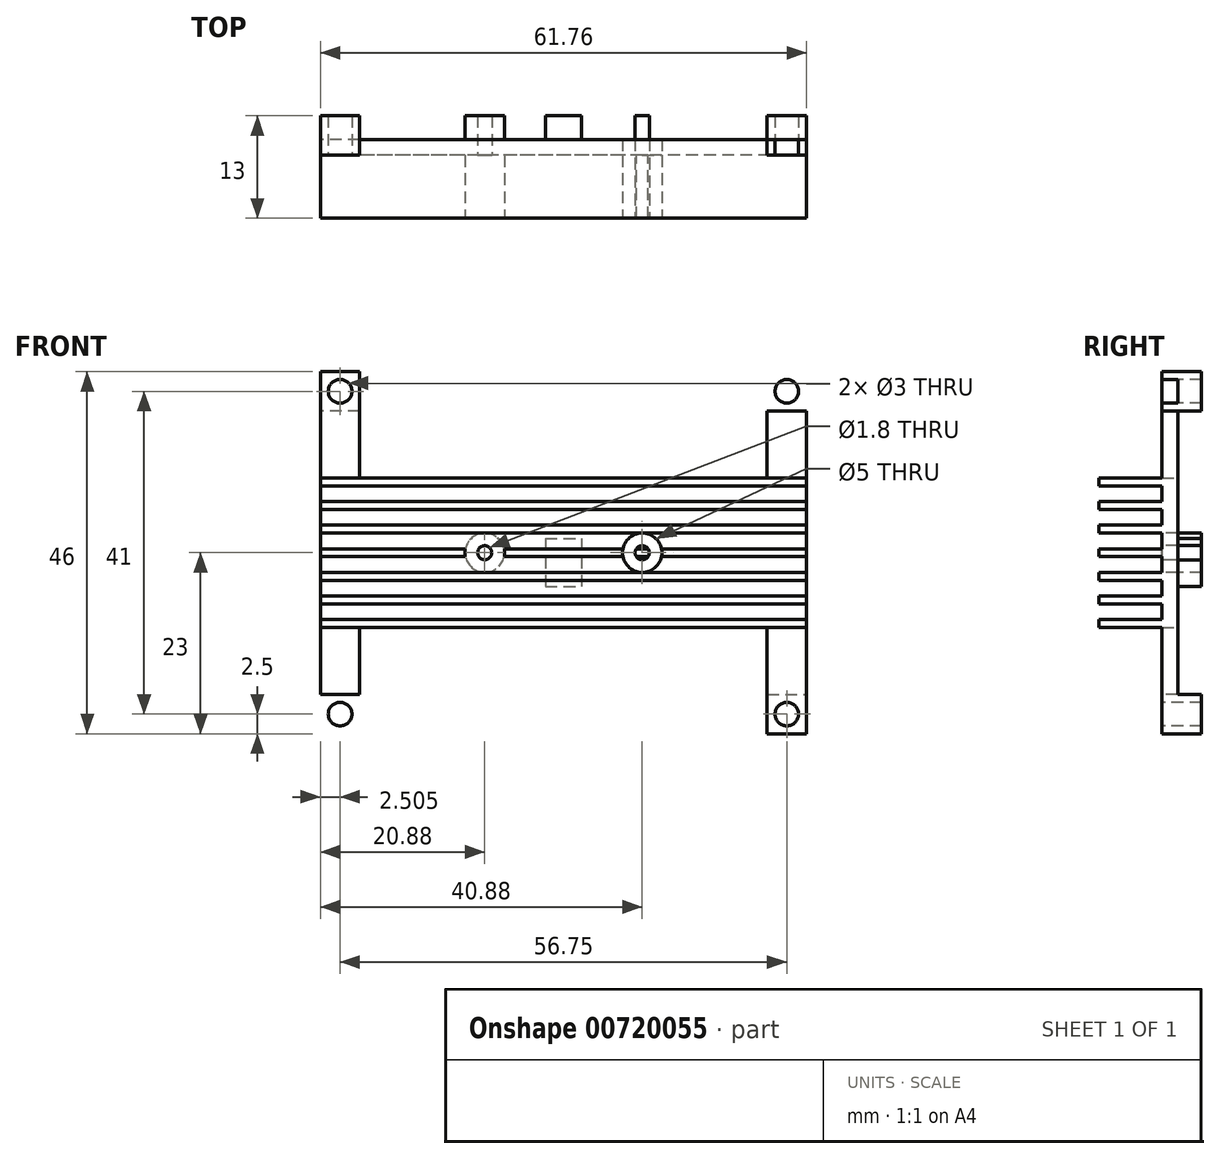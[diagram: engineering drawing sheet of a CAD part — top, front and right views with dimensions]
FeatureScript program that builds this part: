
annotation { "Feature Type Name" : "Feature", "Feature Type Description" : "" }
export const myFeature = defineFeature(function(context is Context, id is Id, definition is map)
    precondition{}
    {
        {
            var Q0;
            Q0=qCreatedBy(makeId("Front.planeOp"),FACE);
            var sketch = newSketch(context, id + "F0", { "sketchPlane" : qUnion([Q0])});
            skLineSegment(sketch, "E0", {"start": v(0, 0) * mm, "end": v(-30.88, 0) * mm, "construction": true});
            skLineSegment(sketch, "E1", {"start": v(-30.88, 0) * mm, "end": v(-30.88, 23) * mm, "construction": true});
            skLineSegment(sketch, "E2.bottom", {"start": v(-30.88, 23) * mm, "end": v(30.88, 23) * mm});
            skLineSegment(sketch, "E2.top", {"start": v(-30.88, -23) * mm, "end": v(30.88, -23) * mm});
            skLineSegment(sketch, "E2.left", {"start": v(-30.88, 23) * mm, "end": v(-30.88, -23) * mm});
            skLineSegment(sketch, "E2.right", {"start": v(30.88, 23) * mm, "end": v(30.88, -23) * mm});
            skPoint(sketch, "E2.middle", {"position": v(0, 0) * mm});
            skLineSegment(sketch, "E3", {"start": v(0, 0) * mm, "end": v(25.88, 0) * mm, "construction": true});
            skLineSegment(sketch, "E4", {"start": v(25.88, 0) * mm, "end": v(25.88, 9.5) * mm, "construction": true});
            skLineSegment(sketch, "E5", {"start": v(25.88, 9.5) * mm, "end": v(25.88, 23) * mm});
            skLineSegment(sketch, "E6", {"start": v(25.87, 9.5) * mm, "end": v(0, 9.5) * mm});
            skLineSegment(sketch, "E7.MirrorCS", {"start": v(-25.88, 9.5) * mm, "end": v(-25.88, 23) * mm});
            skLineSegment(sketch, "E8.MirrorCS", {"start": v(-25.87, 9.5) * mm, "end": v(0, 9.5) * mm});
            skLineSegment(sketch, "E9.MirrorCS", {"start": v(-25.88, -9.5) * mm, "end": v(-25.87, -23) * mm});
            skLineSegment(sketch, "E10.MirrorCS", {"start": v(-25.87, -9.5) * mm, "end": v(0, -9.5) * mm});
            skLineSegment(sketch, "E11.MirrorCS", {"start": v(25.88, -9.5) * mm, "end": v(25.88, -23) * mm});
            skLineSegment(sketch, "E12.MirrorCS", {"start": v(25.87, -9.5) * mm, "end": v(0, -9.5) * mm});
            skSolve(sketch);
        }
        {
            var Q0;
            Q0=makeQuery(id+"F0.imprint","IMPRINT",FACE,{"disambiguationData":[TD([[makeQuery(id+"F0.imprint","IMPRINT",EDGE,{"derivedFrom":sQuery(id+"F0.wireOp",EDGE,"E2.bottom")}),-1.0]])]});
            extrude(context, id + "F1", {"entities" : qUnion([Q0]), "depth" : 10 * mm, "offsetDistance" : 25 * mm});
        }
        {
            var Q0;
            Q0=makeQuery(id+"F1.opExtrude","CAP_FACE",FACE,{"disambiguationData":[OSD([sQuery(id+"F0.wireOp",EDGE,"E2.bottom"),sQuery(id+"F0.wireOp",EDGE,"E2.top"),sQuery(id+"F0.wireOp",EDGE,"E2.left"),sQuery(id+"F0.wireOp",EDGE,"E2.right")])],"isStart":false});
            var sketch = newSketch(context, id + "F2", { "sketchPlane" : qUnion([Q0])});
            skLineSegment(sketch, "E13", {"start": v(-30.88, 0) * mm, "end": v(-30.88, 0.5) * mm, "construction": true});
            skLineSegment(sketch, "E14.bottom", {"start": v(-30.88, 0.5) * mm, "end": v(30.88, 0.5) * mm});
            skLineSegment(sketch, "E14.top", {"start": v(-30.88, -0.5) * mm, "end": v(30.88, -0.5) * mm});
            skLineSegment(sketch, "E14.left", {"start": v(-30.88, 0.5) * mm, "end": v(-30.88, -0.5) * mm});
            skLineSegment(sketch, "E14.right", {"start": v(30.88, 0.5) * mm, "end": v(30.88, -0.5) * mm});
            skPoint(sketch, "E14.middle", {"position": v(0, 0) * mm});
            skLineSegment(sketch, "E15.0.1.0", {"start": v(-30.88, 3.5) * mm, "end": v(30.88, 3.5) * mm});
            skLineSegment(sketch, "E15.0.1.1", {"start": v(-30.88, 3.5) * mm, "end": v(-30.88, 2.5) * mm});
            skLineSegment(sketch, "E15.0.1.2", {"start": v(-30.88, 2.5) * mm, "end": v(30.88, 2.5) * mm});
            skLineSegment(sketch, "E15.0.1.3", {"start": v(30.88, 3.5) * mm, "end": v(30.88, 2.5) * mm});
            skLineSegment(sketch, "E15.0.2.0", {"start": v(-30.88, 6.5) * mm, "end": v(30.88, 6.5) * mm});
            skLineSegment(sketch, "E15.0.2.1", {"start": v(-30.88, 6.5) * mm, "end": v(-30.88, 5.5) * mm});
            skLineSegment(sketch, "E15.0.2.2", {"start": v(-30.88, 5.5) * mm, "end": v(30.88, 5.5) * mm});
            skLineSegment(sketch, "E15.0.2.3", {"start": v(30.88, 6.5) * mm, "end": v(30.88, 5.5) * mm});
            skLineSegment(sketch, "E15.direction1", {"start": v(-30.88, 0.5) * mm, "end": v(-25, 0.5) * mm, "construction": true});
            skLineSegment(sketch, "E15.direction2", {"start": v(-30.88, 0.5) * mm, "end": v(-30.88, 3.5) * mm, "construction": true});
            skLineSegment(sketch, "E16.0.1.0", {"start": v(-30.88, -2.5) * mm, "end": v(30.88, -2.5) * mm});
            skLineSegment(sketch, "E16.0.1.1", {"start": v(-30.88, -2.5) * mm, "end": v(-30.88, -3.5) * mm});
            skLineSegment(sketch, "E16.0.1.2", {"start": v(-30.88, -3.5) * mm, "end": v(30.88, -3.5) * mm});
            skLineSegment(sketch, "E16.0.1.3", {"start": v(30.88, -2.5) * mm, "end": v(30.88, -3.5) * mm});
            skLineSegment(sketch, "E16.0.2.0", {"start": v(-30.88, -5.5) * mm, "end": v(30.88, -5.5) * mm});
            skLineSegment(sketch, "E16.0.2.1", {"start": v(-30.88, -5.5) * mm, "end": v(-30.88, -6.5) * mm});
            skLineSegment(sketch, "E16.0.2.2", {"start": v(-30.88, -6.5) * mm, "end": v(30.88, -6.5) * mm});
            skLineSegment(sketch, "E16.0.2.3", {"start": v(30.88, -5.5) * mm, "end": v(30.88, -6.5) * mm});
            skLineSegment(sketch, "E16.direction2", {"start": v(-30.88, 0.5) * mm, "end": v(-30.88, -2.5) * mm, "construction": true});
            skLineSegment(sketch, "E17.0.0.3", {"start": v(-30.88, 9.5) * mm, "end": v(30.88, 9.5) * mm});
            skLineSegment(sketch, "E17.3.0.3", {"start": v(-30.88, 9.5) * mm, "end": v(-30.88, 8.5) * mm});
            skLineSegment(sketch, "E17.6.0.3", {"start": v(-30.88, 8.5) * mm, "end": v(30.88, 8.5) * mm});
            skLineSegment(sketch, "E17.9.0.3", {"start": v(30.88, 9.5) * mm, "end": v(30.88, 8.5) * mm});
            skLineSegment(sketch, "E18.0.0.3", {"start": v(-30.88, -8.5) * mm, "end": v(30.88, -8.5) * mm});
            skLineSegment(sketch, "E18.3.0.3", {"start": v(-30.88, -8.5) * mm, "end": v(-30.88, -9.5) * mm});
            skLineSegment(sketch, "E18.6.0.3", {"start": v(-30.88, -9.5) * mm, "end": v(30.88, -9.5) * mm});
            skLineSegment(sketch, "E18.9.0.3", {"start": v(30.88, -8.5) * mm, "end": v(30.88, -9.5) * mm});
            skSolve(sketch);
        }
        {
            var Q0;
            Q0=qCreatedBy(makeId("Front.planeOp"),FACE);
            cPlane(context, id + "F3", {"entities" : qUnion([Q0]), "cplaneType" : CPlaneType.OFFSET, "offset" : 2 * mm, "width" : 150 * mm, "height" : 150 * mm});
        }
        {
            var Q0;
            {var subQ1=sQuery(id+"F0.wireOp",EDGE,"E7.MirrorCS");var subQ2=makeQuery(id+"F1.opExtrude","CAP_EDGE",EDGE,{"disambiguationData":[OSD([subQ1])],"isStart":false});Q0=makeQuery(id+"F2.imprint","IMPRINT",FACE,{"disambiguationData":[TD([[makeQuery(id+"F2.imprint","IMPRINT",EDGE,{"derivedFrom":subQ2}),1.0]])]});}
            var Q1;
            {var subQ0=sQuery(id+"F2.wireOp",EDGE,"E15.0.2.0");Q1=makeQuery(id+"F2.imprint","IMPRINT",FACE,{"disambiguationData":[TD([[makeQuery(id+"F2.imprint","IMPRINT",EDGE,{"derivedFrom":subQ0}),1.0]])]});}
            var Q2;
            {var subQ0=sQuery(id+"F2.wireOp",EDGE,"E15.0.1.0");Q2=makeQuery(id+"F2.imprint","IMPRINT",FACE,{"disambiguationData":[TD([[makeQuery(id+"F2.imprint","IMPRINT",EDGE,{"derivedFrom":subQ0}),1.0]])]});}
            var Q3;
            {var subQ0=sQuery(id+"F2.wireOp",EDGE,"E14.bottom");Q3=makeQuery(id+"F2.imprint","IMPRINT",FACE,{"disambiguationData":[TD([[makeQuery(id+"F2.imprint","IMPRINT",EDGE,{"derivedFrom":subQ0}),1.0]])]});}
            var Q4;
            {var subQ0=sQuery(id+"F2.wireOp",EDGE,"E14.top");Q4=makeQuery(id+"F2.imprint","IMPRINT",FACE,{"disambiguationData":[TD([[makeQuery(id+"F2.imprint","IMPRINT",EDGE,{"derivedFrom":subQ0}),-1.0]])]});}
            var Q5;
            {var subQ0=sQuery(id+"F2.wireOp",EDGE,"E16.0.1.2");Q5=makeQuery(id+"F2.imprint","IMPRINT",FACE,{"disambiguationData":[TD([[makeQuery(id+"F2.imprint","IMPRINT",EDGE,{"derivedFrom":subQ0}),-1.0]])]});}
            var Q6;
            {var subQ0=sQuery(id+"F2.wireOp",EDGE,"E16.0.2.2");Q6=makeQuery(id+"F2.imprint","IMPRINT",FACE,{"disambiguationData":[TD([[makeQuery(id+"F2.imprint","IMPRINT",EDGE,{"derivedFrom":subQ0}),-1.0]])]});}
            var Q7;
            {var subQ1=sQuery(id+"F0.wireOp",EDGE,"E9.MirrorCS");var subQ2=makeQuery(id+"F1.opExtrude","CAP_EDGE",EDGE,{"disambiguationData":[OSD([subQ1])],"isStart":false});Q7=makeQuery(id+"F2.imprint","IMPRINT",FACE,{"disambiguationData":[TD([[makeQuery(id+"F2.imprint","IMPRINT",EDGE,{"derivedFrom":subQ2}),-1.0]])]});}
            var Q8;
            {var subQ1=sQuery(id+"F0.wireOp",EDGE,"E5");var subQ2=makeQuery(id+"F1.opExtrude","CAP_EDGE",EDGE,{"disambiguationData":[OSD([subQ1])],"isStart":false});Q8=makeQuery(id+"F2.imprint","IMPRINT",FACE,{"disambiguationData":[TD([[makeQuery(id+"F2.imprint","IMPRINT",EDGE,{"derivedFrom":subQ2}),-1.0]])]});}
            var Q9;
            {var subQ1=sQuery(id+"F0.wireOp",EDGE,"E11.MirrorCS");var subQ2=makeQuery(id+"F1.opExtrude","CAP_EDGE",EDGE,{"disambiguationData":[OSD([subQ1])],"isStart":false});Q9=makeQuery(id+"F2.imprint","IMPRINT",FACE,{"disambiguationData":[TD([[makeQuery(id+"F2.imprint","IMPRINT",EDGE,{"derivedFrom":subQ2}),1.0]])]});}
            var Q10;
            Q10=qCreatedBy(id+"F3.planeOp",FACE);
            extrude(context, id + "F4", {"entities" : qUnion([Q0, Q1, Q2, Q3, Q4, Q5, Q6, Q7, Q8, Q9]), "operationType" : NewBodyOperationType.REMOVE, "endBound" : BoundingType.UP_TO_SURFACE, "oppositeDirection" : true, "depth" : 25 * mm, "endBoundEntityFace" : qUnion([Q10]), "offsetDistance" : 25 * mm});
        }
        {
            var Q0;
            Q0=qCreatedBy(id+"F3.planeOp",FACE);
            var sketch = newSketch(context, id + "F5", { "sketchPlane" : qUnion([Q0])});
            skLineSegment(sketch, "E19", {"start": v(0, 0) * mm, "end": v(-10, 0) * mm, "construction": true});
            skLineSegment(sketch, "E20", {"start": v(0, 0) * mm, "end": v(-2.3, 0) * mm, "construction": true});
            skLineSegment(sketch, "E21", {"start": v(-2.3, 0) * mm, "end": v(-2.3, 1.8) * mm, "construction": true});
            skLineSegment(sketch, "E22", {"start": v(0, 0) * mm, "end": v(2.3, 0) * mm, "construction": true});
            skLineSegment(sketch, "E23", {"start": v(2.3, 0) * mm, "end": v(2.3, -4.3) * mm, "construction": true});
            skLineSegment(sketch, "E24.bottom", {"start": v(-2.3, 1.8) * mm, "end": v(2.3, 1.8) * mm});
            skLineSegment(sketch, "E24.top", {"start": v(-2.3, -4.3) * mm, "end": v(2.3, -4.3) * mm});
            skLineSegment(sketch, "E24.left", {"start": v(-2.3, 1.8) * mm, "end": v(-2.3, -4.3) * mm});
            skLineSegment(sketch, "E24.right", {"start": v(2.3, 1.8) * mm, "end": v(2.3, -4.3) * mm});
            skCircle(sketch, "E25", {"center": v(-10, 0) * mm, "radius": 0.9 * mm});
            skCircle(sketch, "E26", {"center": v(-10, 0) * mm, "radius": 2.5 * mm});
            skLineSegment(sketch, "E27.bottom", {"start": v(-7.5, 2.5) * mm, "end": v(-12.5, 2.5) * mm});
            skLineSegment(sketch, "E27.top", {"start": v(-7.5, -2.5) * mm, "end": v(-12.5, -2.5) * mm});
            skLineSegment(sketch, "E27.left", {"start": v(-7.5, 2.5) * mm, "end": v(-7.5, -2.5) * mm});
            skLineSegment(sketch, "E27.right", {"start": v(-12.5, 2.5) * mm, "end": v(-12.5, -2.5) * mm});
            skLineSegment(sketch, "E28.MirrorCS", {"start": v(7.5, 2.5) * mm, "end": v(7.5, -2.5) * mm});
            skLineSegment(sketch, "E29.MirrorCS", {"start": v(7.5, 2.5) * mm, "end": v(12.5, 2.5) * mm});
            skCircle(sketch, "E30.MirrorC", {"center": v(10, 0) * mm, "radius": 2.5 * mm});
            skCircle(sketch, "E31.MirrorC", {"center": v(10, 0) * mm, "radius": 0.9 * mm});
            skLineSegment(sketch, "E32.MirrorCS", {"start": v(7.5, -2.5) * mm, "end": v(12.5, -2.5) * mm});
            skLineSegment(sketch, "E33.MirrorCS", {"start": v(12.5, 2.5) * mm, "end": v(12.5, -2.5) * mm});
            skLineSegment(sketch, "E34", {"start": v(0, 0) * mm, "end": v(0, 20.5) * mm, "construction": true});
            skLineSegment(sketch, "E35", {"start": v(0, 20.5) * mm, "end": v(-28.38, 20.5) * mm, "construction": true});
            skCircle(sketch, "E36", {"center": v(-28.38, 20.5) * mm, "radius": 1.5 * mm});
            skLineSegment(sketch, "E37.bottom", {"start": v(-25.87, 23) * mm, "end": v(-30.87, 23) * mm});
            skLineSegment(sketch, "E37.top", {"start": v(-25.88, 18) * mm, "end": v(-30.88, 18) * mm});
            skLineSegment(sketch, "E37.left", {"start": v(-25.88, 23) * mm, "end": v(-25.88, 18) * mm});
            skLineSegment(sketch, "E37.right", {"start": v(-30.88, 23) * mm, "end": v(-30.88, 18) * mm});
            skLineSegment(sketch, "E38.MirrorCS", {"start": v(25.88, 23) * mm, "end": v(25.88, 18) * mm});
            skLineSegment(sketch, "E39.MirrorCS", {"start": v(25.88, 18) * mm, "end": v(30.88, 18) * mm});
            skLineSegment(sketch, "E40.MirrorCS", {"start": v(30.88, 23) * mm, "end": v(30.88, 18) * mm});
            skLineSegment(sketch, "E41.MirrorCS", {"start": v(25.87, 23) * mm, "end": v(30.87, 23) * mm});
            skCircle(sketch, "E42.MirrorC", {"center": v(28.38, 20.5) * mm, "radius": 1.5 * mm});
            skCircle(sketch, "E43.MirrorC", {"center": v(-28.38, -20.5) * mm, "radius": 1.5 * mm});
            skLineSegment(sketch, "E44.MirrorCS", {"start": v(-25.88, -23) * mm, "end": v(-25.88, -18) * mm});
            skLineSegment(sketch, "E45.MirrorCS", {"start": v(-25.88, -18) * mm, "end": v(-30.88, -18) * mm});
            skLineSegment(sketch, "E46.MirrorCS", {"start": v(-30.88, -23) * mm, "end": v(-30.88, -18) * mm});
            skLineSegment(sketch, "E47.MirrorCS", {"start": v(-25.87, -23) * mm, "end": v(-30.87, -23) * mm});
            skCircle(sketch, "E48.MirrorC", {"center": v(28.38, -20.5) * mm, "radius": 1.5 * mm});
            skLineSegment(sketch, "E49.MirrorCS", {"start": v(25.87, -23) * mm, "end": v(30.87, -23) * mm});
            skLineSegment(sketch, "E50.MirrorCS", {"start": v(30.88, -23) * mm, "end": v(30.88, -18) * mm});
            skLineSegment(sketch, "E51.MirrorCS", {"start": v(25.88, -18) * mm, "end": v(30.88, -18) * mm});
            skLineSegment(sketch, "E52.MirrorCS", {"start": v(25.88, -23) * mm, "end": v(25.88, -18) * mm});
            skSolve(sketch);
        }
        {
            var Q0;
            Q0=makeQuery(id+"F1.opExtrude","CAP_FACE",FACE,{"disambiguationData":[OSD([sQuery(id+"F0.wireOp",EDGE,"E2.bottom"),sQuery(id+"F0.wireOp",EDGE,"E2.top"),sQuery(id+"F0.wireOp",EDGE,"E2.left"),sQuery(id+"F0.wireOp",EDGE,"E2.right")])],"isStart":true});
            cPlane(context, id + "F6", {"entities" : qUnion([Q0]), "cplaneType" : CPlaneType.OFFSET, "offset" : 3 * mm, "width" : 150 * mm, "height" : 150 * mm});
        }
        {
            var Q0;
            Q0=makeQuery(id+"F5.imprint","IMPRINT",FACE,{"disambiguationData":[TD([[makeQuery(id+"F5.imprint","IMPRINT",EDGE,{"derivedFrom":sQuery(id+"F5.wireOp",EDGE,"E36")}),-1.0]])]});
            var Q1;
            Q1=makeQuery(id+"F5.imprint","IMPRINT",FACE,{"disambiguationData":[TD([[makeQuery(id+"F5.imprint","IMPRINT",EDGE,{"derivedFrom":sQuery(id+"F5.wireOp",EDGE,"E38.MirrorCS")}),1.0]])]});
            var Q2;
            Q2=makeQuery(id+"F5.imprint","IMPRINT",FACE,{"disambiguationData":[TD([[makeQuery(id+"F5.imprint","IMPRINT",EDGE,{"derivedFrom":sQuery(id+"F5.wireOp",EDGE,"E48.MirrorC")}),-1.0]])]});
            var Q3;
            Q3=makeQuery(id+"F5.imprint","IMPRINT",FACE,{"disambiguationData":[TD([[makeQuery(id+"F5.imprint","IMPRINT",EDGE,{"derivedFrom":sQuery(id+"F5.wireOp",EDGE,"E43.MirrorC")}),1.0]])]});
            var Q4;
            Q4=makeQuery(id+"F5.imprint","IMPRINT",FACE,{"disambiguationData":[TD([[makeQuery(id+"F5.imprint","IMPRINT",EDGE,{"derivedFrom":sQuery(id+"F5.wireOp",EDGE,"E31.MirrorC")}),1.0]])]});
            var Q5;
            Q5=makeQuery(id+"F5.imprint","IMPRINT",FACE,{"disambiguationData":[TD([[makeQuery(id+"F5.imprint","IMPRINT",EDGE,{"derivedFrom":sQuery(id+"F5.wireOp",EDGE,"E25")}),-1.0]])]});
            var Q6;
            Q6=makeQuery(id+"F5.imprint","IMPRINT",FACE,{"disambiguationData":[TD([[makeQuery(id+"F5.imprint","IMPRINT",EDGE,{"derivedFrom":sQuery(id+"F5.wireOp",EDGE,"E24.bottom")}),-1.0]])]});
            var Q7;
            Q7=qCreatedBy(id+"F6.planeOp",FACE);
            extrude(context, id + "F7", {"entities" : qUnion([Q0, Q1, Q2, Q3, Q4, Q5, Q6]), "operationType" : NewBodyOperationType.ADD, "endBound" : BoundingType.UP_TO_SURFACE, "oppositeDirection" : true, "depth" : 25 * mm, "endBoundEntityFace" : qUnion([Q7]), "offsetDistance" : 25 * mm});
        }
        {
            var Q0;
            Q0=makeQuery(id+"F5.imprint","IMPRINT",FACE,{"disambiguationData":[TD([[makeQuery(id+"F5.imprint","IMPRINT",EDGE,{"derivedFrom":sQuery(id+"F5.wireOp",EDGE,"jt35dyTl-ikho-eOT0-DAPU-rAh0OH2Ca2D4")}),-1.0]])]});
            var Q1;
            Q1=makeQuery(id+"F5.imprint","IMPRINT",FACE,{"disambiguationData":[TD([[makeQuery(id+"F5.imprint","IMPRINT",EDGE,{"derivedFrom":sQuery(id+"F5.wireOp",EDGE,"NUw0Rw4t-io0l-YQbQ-xWhD-a46VIXt3r54f")}),-1.0]])]});
            var Q2;
            Q2=makeQuery(id+"F5.imprint","IMPRINT",FACE,{"disambiguationData":[TD([[makeQuery(id+"F5.imprint","IMPRINT",EDGE,{"derivedFrom":sQuery(id+"F5.wireOp",EDGE,"NUw0Rw4t-io0l-YQbQ-xWhD-a46VIXt3r54f")}),1.0]])]});
            var Q3;
            Q3=makeQuery(id+"F5.imprint","IMPRINT",FACE,{"disambiguationData":[TD([[makeQuery(id+"F5.imprint","IMPRINT",EDGE,{"derivedFrom":sQuery(id+"F5.wireOp",EDGE,"03f16da8-e4e8-4d85-aba3-7918eac5e81c.1.0.0")}),1.0]])]});
            var Q4;
            Q4=makeQuery(id+"F5.imprint","IMPRINT",FACE,{"disambiguationData":[TD([[makeQuery(id+"F5.imprint","IMPRINT",EDGE,{"derivedFrom":sQuery(id+"F5.wireOp",EDGE,"03f16da8-e4e8-4d85-aba3-7918eac5e81c.1.0.4")}),1.0]])]});
            var Q5;
            Q5=makeQuery(id+"F5.imprint","IMPRINT",FACE,{"disambiguationData":[TD([[makeQuery(id+"F5.imprint","IMPRINT",EDGE,{"derivedFrom":sQuery(id+"F5.wireOp",EDGE,"03f16da8-e4e8-4d85-aba3-7918eac5e81c.1.0.5")}),1.0]])]});
            var Q6;
            Q6=makeQuery(id+"F5.imprint","IMPRINT",FACE,{"disambiguationData":[TD([[makeQuery(id+"F5.imprint","IMPRINT",EDGE,{"derivedFrom":sQuery(id+"F5.wireOp",EDGE,"03f16da8-e4e8-4d85-aba3-7918eac5e81c.0.1.0")}),1.0]])]});
            var Q7;
            Q7=makeQuery(id+"F5.imprint","IMPRINT",FACE,{"disambiguationData":[TD([[makeQuery(id+"F5.imprint","IMPRINT",EDGE,{"derivedFrom":sQuery(id+"F5.wireOp",EDGE,"03f16da8-e4e8-4d85-aba3-7918eac5e81c.0.1.4")}),1.0]])]});
            var Q8;
            Q8=makeQuery(id+"F5.imprint","IMPRINT",FACE,{"disambiguationData":[TD([[makeQuery(id+"F5.imprint","IMPRINT",EDGE,{"derivedFrom":sQuery(id+"F5.wireOp",EDGE,"03f16da8-e4e8-4d85-aba3-7918eac5e81c.0.1.5")}),1.0]])]});
            var Q9;
            Q9=makeQuery(id+"F5.imprint","IMPRINT",FACE,{"disambiguationData":[TD([[makeQuery(id+"F5.imprint","IMPRINT",EDGE,{"derivedFrom":sQuery(id+"F5.wireOp",EDGE,"03f16da8-e4e8-4d85-aba3-7918eac5e81c.1.1.0")}),1.0]])]});
            var Q10;
            Q10=makeQuery(id+"F5.imprint","IMPRINT",FACE,{"disambiguationData":[TD([[makeQuery(id+"F5.imprint","IMPRINT",EDGE,{"derivedFrom":sQuery(id+"F5.wireOp",EDGE,"03f16da8-e4e8-4d85-aba3-7918eac5e81c.1.1.4")}),1.0]])]});
            var Q11;
            Q11=makeQuery(id+"F5.imprint","IMPRINT",FACE,{"disambiguationData":[TD([[makeQuery(id+"F5.imprint","IMPRINT",EDGE,{"derivedFrom":sQuery(id+"F5.wireOp",EDGE,"03f16da8-e4e8-4d85-aba3-7918eac5e81c.1.1.5")}),1.0]])]});
            var Q12;
            Q12=makeQuery(id+"F5.imprint","IMPRINT",FACE,{"disambiguationData":[TD([[makeQuery(id+"F5.imprint","IMPRINT",EDGE,{"derivedFrom":sQuery(id+"F5.wireOp",EDGE,"ad8dfa2b-27ac-4793-8de9-5985fa3aa7040.MirrorC")}),1.0]])]});
            var Q13;
            Q13=makeQuery(id+"F5.imprint","IMPRINT",FACE,{"disambiguationData":[TD([[makeQuery(id+"F5.imprint","IMPRINT",EDGE,{"derivedFrom":sQuery(id+"F5.wireOp",EDGE,"ad8dfa2b-27ac-4793-8de9-5985fa3aa7040.MirrorC")}),-1.0]])]});
            var Q14;
            Q14=makeQuery(id+"F5.imprint","IMPRINT",FACE,{"disambiguationData":[TD([[makeQuery(id+"F5.imprint","IMPRINT",EDGE,{"derivedFrom":sQuery(id+"F5.wireOp",EDGE,"8f5c5904-3a9c-41bb-bb4c-c44c0577cf6c0.MirrorC")}),-1.0]])]});
            var Q15;
            Q15=makeQuery(id+"F5.imprint","IMPRINT",FACE,{"disambiguationData":[TD([[makeQuery(id+"F5.imprint","IMPRINT",EDGE,{"derivedFrom":sQuery(id+"F5.wireOp",EDGE,"79443795-5f22-4850-96de-6a89882279580.MirrorC")}),1.0]])]});
            var Q16;
            Q16=makeQuery(id+"F5.imprint","IMPRINT",FACE,{"disambiguationData":[TD([[makeQuery(id+"F5.imprint","IMPRINT",EDGE,{"derivedFrom":sQuery(id+"F5.wireOp",EDGE,"79443795-5f22-4850-96de-6a89882279580.MirrorC")}),-1.0]])]});
            var Q17;
            Q17=makeQuery(id+"F5.imprint","IMPRINT",FACE,{"disambiguationData":[TD([[makeQuery(id+"F5.imprint","IMPRINT",EDGE,{"derivedFrom":sQuery(id+"F5.wireOp",EDGE,"115d48f7-b85f-44a2-8c5e-97de7b7ec2c00.MirrorC")}),-1.0]])]});
            var Q18;
            Q18=makeQuery(id+"F5.imprint","IMPRINT",FACE,{"disambiguationData":[TD([[makeQuery(id+"F5.imprint","IMPRINT",EDGE,{"derivedFrom":sQuery(id+"F5.wireOp",EDGE,"4b71248d-8159-4820-aea2-80c2b7ea0b7d0.MirrorC")}),1.0]])]});
            var Q19;
            Q19=makeQuery(id+"F5.imprint","IMPRINT",FACE,{"disambiguationData":[TD([[makeQuery(id+"F5.imprint","IMPRINT",EDGE,{"derivedFrom":sQuery(id+"F5.wireOp",EDGE,"4b71248d-8159-4820-aea2-80c2b7ea0b7d0.MirrorC")}),-1.0]])]});
            var Q20;
            Q20=makeQuery(id+"F5.imprint","IMPRINT",FACE,{"disambiguationData":[TD([[makeQuery(id+"F5.imprint","IMPRINT",EDGE,{"derivedFrom":sQuery(id+"F5.wireOp",EDGE,"2becf76c-0659-440b-acd6-233aa11e40930.MirrorC")}),-1.0]])]});
            var Q21;
            Q21=makeQuery(id+"F5.imprint","IMPRINT",FACE,{"disambiguationData":[TD([[makeQuery(id+"F5.imprint","IMPRINT",EDGE,{"derivedFrom":sQuery(id+"F5.wireOp",EDGE,"404a5a20-5de5-4e40-a993-ef5180606b200.MirrorC")}),1.0]])]});
            var Q22;
            Q22=makeQuery(id+"F5.imprint","IMPRINT",FACE,{"disambiguationData":[TD([[makeQuery(id+"F5.imprint","IMPRINT",EDGE,{"derivedFrom":sQuery(id+"F5.wireOp",EDGE,"404a5a20-5de5-4e40-a993-ef5180606b200.MirrorC")}),-1.0]])]});
            var Q23;
            Q23=makeQuery(id+"F5.imprint","IMPRINT",FACE,{"disambiguationData":[TD([[makeQuery(id+"F5.imprint","IMPRINT",EDGE,{"derivedFrom":sQuery(id+"F5.wireOp",EDGE,"aca2cda7-5277-44f8-8964-53229556d0ad0.MirrorC")}),-1.0]])]});
            var Q24;
            Q24=makeQuery(id+"F5.imprint","IMPRINT",FACE,{"disambiguationData":[TD([[makeQuery(id+"F5.imprint","IMPRINT",EDGE,{"derivedFrom":sQuery(id+"F5.wireOp",EDGE,"E26")}),-1.0]])]});
            var Q25;
            Q25=makeQuery(id+"F5.imprint","IMPRINT",FACE,{"disambiguationData":[TD([[makeQuery(id+"F5.imprint","IMPRINT",EDGE,{"derivedFrom":sQuery(id+"F5.wireOp",EDGE,"E25")}),-1.0]])]});
            var Q26;
            Q26=makeQuery(id+"F5.imprint","IMPRINT",FACE,{"disambiguationData":[TD([[makeQuery(id+"F5.imprint","IMPRINT",EDGE,{"derivedFrom":sQuery(id+"F5.wireOp",EDGE,"E25")}),1.0]])]});
            var Q27;
            Q27=makeQuery(id+"F5.imprint","IMPRINT",FACE,{"disambiguationData":[TD([[makeQuery(id+"F5.imprint","IMPRINT",EDGE,{"derivedFrom":sQuery(id+"F5.wireOp",EDGE,"E28.MirrorCS")}),1.0]])]});
            var Q28;
            Q28=makeQuery(id+"F5.imprint","IMPRINT",FACE,{"disambiguationData":[TD([[makeQuery(id+"F5.imprint","IMPRINT",EDGE,{"derivedFrom":sQuery(id+"F5.wireOp",EDGE,"E30.MirrorC")}),-1.0]])]});
            var Q29;
            Q29=makeQuery(id+"F5.imprint","IMPRINT",FACE,{"disambiguationData":[TD([[makeQuery(id+"F5.imprint","IMPRINT",EDGE,{"derivedFrom":sQuery(id+"F5.wireOp",EDGE,"E31.MirrorC")}),-1.0]])]});
            extrude(context, id + "F8", {"entities" : qUnion([Q0, Q1, Q2, Q3, Q4, Q5, Q6, Q7, Q8, Q9, Q10, Q11, Q12, Q13, Q14, Q15, Q16, Q17, Q18, Q19, Q20, Q21, Q22, Q23, Q24, Q25, Q26, Q27, Q28, Q29]), "operationType" : NewBodyOperationType.REMOVE, "endBound" : BoundingType.THROUGH_ALL, "depth" : 25 * mm, "offsetDistance" : 25 * mm});
        }
        {
            var Q0;
            Q0=makeQuery(id+"F5.imprint","IMPRINT",FACE,{"disambiguationData":[TD([[makeQuery(id+"F5.imprint","IMPRINT",EDGE,{"derivedFrom":sQuery(id+"F5.wireOp",EDGE,"E42.MirrorC")}),-1.0]])]});
            var Q1;
            Q1=makeQuery(id+"F5.imprint","IMPRINT",FACE,{"disambiguationData":[TD([[makeQuery(id+"F5.imprint","IMPRINT",EDGE,{"derivedFrom":sQuery(id+"F5.wireOp",EDGE,"E31.MirrorC")}),-1.0]])]});
            var Q2;
            Q2=makeQuery(id+"F5.imprint","IMPRINT",FACE,{"disambiguationData":[TD([[makeQuery(id+"F5.imprint","IMPRINT",EDGE,{"derivedFrom":sQuery(id+"F5.wireOp",EDGE,"E25")}),1.0]])]});
            var Q3;
            Q3=makeQuery(id+"F5.imprint","IMPRINT",FACE,{"disambiguationData":[TD([[makeQuery(id+"F5.imprint","IMPRINT",EDGE,{"derivedFrom":sQuery(id+"F5.wireOp",EDGE,"E48.MirrorC")}),1.0]])]});
            var Q4;
            Q4=makeQuery(id+"F5.imprint","IMPRINT",FACE,{"disambiguationData":[TD([[makeQuery(id+"F5.imprint","IMPRINT",EDGE,{"derivedFrom":sQuery(id+"F5.wireOp",EDGE,"E43.MirrorC")}),-1.0]])]});
            var Q5;
            Q5=makeQuery(id+"F5.imprint","IMPRINT",FACE,{"disambiguationData":[TD([[makeQuery(id+"F5.imprint","IMPRINT",EDGE,{"derivedFrom":sQuery(id+"F5.wireOp",EDGE,"E36")}),1.0]])]});
            extrude(context, id + "F9", {"entities" : qUnion([Q0, Q1, Q2, Q3, Q4, Q5]), "operationType" : NewBodyOperationType.REMOVE, "endBound" : BoundingType.THROUGH_ALL, "oppositeDirection" : true, "depth" : 25 * mm, "offsetDistance" : 25 * mm});
        }
    });
